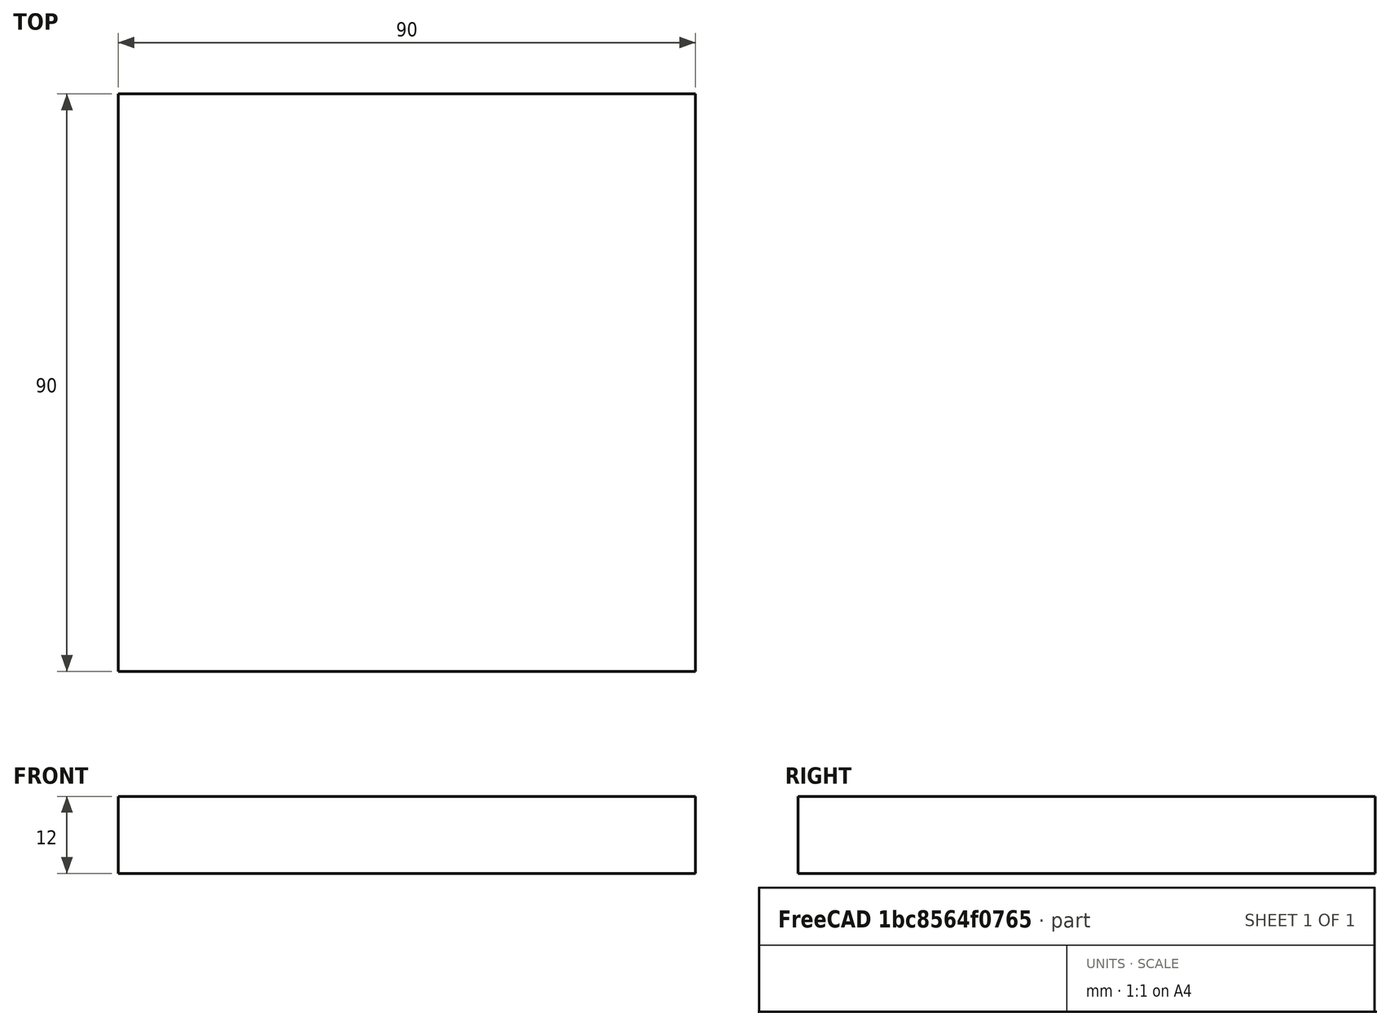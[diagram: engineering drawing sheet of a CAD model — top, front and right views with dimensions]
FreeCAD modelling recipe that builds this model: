
FCSTD DOCUMENT  (FreeCAD 0.18R16146 (Git))
Label: ThreeHoles00
License: All rights reserved
LicenseURL: http://en.wikipedia.org/wiki/All_rights_reserved
objects: Path::FeaturePython×3, Sketcher::SketchObject×2, Part::FeaturePython×2, PartDesign::Pad×1, App::FeaturePython×1, PartDesign::Pocket×1, PartDesign::Body×1, App::DocumentObjectGroup×1, Path::FeatureCompoundPython×1, Mesh::FeaturePython×1
note: 10 computed .brp shape members not serialized (recipe doc carries the construction recipe); baked Part::Feature solids carry a one-line shape summary decoded from their .brp

FEATURE [Sketcher::SketchObject] Sketch
  MapMode = 5
  Support = -> [XY_Plane]
  sketch-geometry (4):
    g0: LineSegment StartX=0 StartY=0 StartZ=0 EndX=70 EndY=0 EndZ=0
    g1: LineSegment StartX=70 StartY=0 StartZ=0 EndX=70 EndY=70 EndZ=0
    g2: LineSegment StartX=70 StartY=70 StartZ=0 EndX=0 EndY=70 EndZ=0
    g3: LineSegment StartX=0 StartY=70 StartZ=0 EndX=0 EndY=0 EndZ=0
  constraints (9):
    c: Coincident(g0,g1)
    c: Coincident(g1,g2)
    c: Coincident(g2,g3)
    c: Coincident(g3,g0)
    c: Horizontal(g0)
    c: Horizontal(g2)
    c: Vertical(g1)
    c: Vertical(g3)
    c: Coincident(g0,g-1)
FEATURE [PartDesign::Pad] Pad
  Length = 10
  Length2 = 100
  Profile = -> Sketch
  Type = 0
FEATURE [App::FeaturePython] SetupSheet  # Path/CAM operation (typed FeaturePython)
  ClearanceHeightExpression = OpStockZMax+SetupSheet.ClearanceHeightOffset
  ClearanceHeightOffset = 5
  FinalDepthExpression = OpFinalDepth
  HorizRapid = 0
  SafeHeightExpression = OpStockZMax+SetupSheet.SafeHeightOffset
  SafeHeightOffset = 3
  StartDepthExpression = OpStartDepth
  StepDownExpression = OpToolDiameter
  VertRapid = 0
FEATURE [Path::FeaturePython] T3__Fraise_6mm  label="T3: Fraise 6mm"  # Path/CAM operation (typed FeaturePython)
  HorizFeed = 5
  HorizRapid = 0
  SpindleDir = 0
  SpindleSpeed = 0
  ToolNumber = 3
  VertFeed = 5
  VertRapid = 0
  expr: HorizRapid = SetupSheet.HorizRapid
  expr: VertRapid = SetupSheet.VertRapid
FEATURE [Sketcher::SketchObject] Sketch001
  MapMode = 5
  Placement = pos=(0,0,10) rot=(0,0,1;0rad)
  Support = -> [Pad]
  sketch-geometry (3):
    g0: Circle CenterX=10 CenterY=20 CenterZ=0 NormalX=0 NormalY=0 NormalZ=1 AngleXU=0 Radius=3.05
    g1: Circle CenterX=10 CenterY=60 CenterZ=0 NormalX=0 NormalY=0 NormalZ=1 AngleXU=0 Radius=3.05
    g2: Circle CenterX=40 CenterY=50 CenterZ=0 NormalX=0 NormalY=0 NormalZ=1 AngleXU=0 Radius=3.05
  constraints (3):
    c: Radius(g0) = 3.05
    c: Equal(g0,g1)
    c: Equal(g0,g2)
FEATURE [PartDesign::Pocket] Pocket
  BaseFeature = -> Pad
  Length = 5
  Length2 = 100
  Profile = -> Sketch001
  Type = 1
FEATURE [PartDesign::Body] Body
  Group = -> [Sketch,Pad,Sketch001,Pocket]
  Origin = -> Origin
  Tip = -> Pocket
FEATURE [Part::FeaturePython] Clone  label="Model-Body"  # Draft clone (typed FeaturePython)
  AttacherType = Attacher::AttachEngine3D
  Fuse = false
  Objects = -> [Body]
  PathResource = Model
  Placement = pos=(10,10,-11) rot=(0,0,1;0rad)
  Scale = (1,1,1)
FEATURE [App::DocumentObjectGroup] Model
  Group = -> [Clone]
FEATURE [Part::FeaturePython] Stock  # WARN: FeaturePython — macro-defined, semantics opaque (R4)
  Base = -> Model
  ExtXneg = 10
  ExtXpos = 10
  ExtYneg = 10
  ExtYpos = 10
  ExtZneg = 1
  ExtZpos = 1
  Placement = pos=(10,10,-11) rot=(0,0,1;0rad)
  StockType = FromBase
FEATURE [Path::FeaturePython] Pocket_Shape  # Path/CAM operation (typed FeaturePython)
  Active = true
  AreaParams:
    Tolerance = 1e-07
    FitArcs = True
    Simplify = False
    CleanDistance = 0.0
    Accuracy = 0.01
    Unit = 1.0
    MinArcPoints = 4
    MaxArcPoints = 100
    ClipperScale = 10000000.0
    Fill = 0
    Coplanar = 0
    Reorient = True
    Outline = False
    Explode = False
    OpenMode = 0
    Deflection = 0.01
    SubjectFill = 0
    ClipFill = 0
    Offset = 0.0
    ExtraPass = 0
    Stepover = 0.0
    LastStepover = 0.0
    JoinType = 0
    EndType = 0
    MiterLimit = 2.0
    RoundPrecision = 0.0
    PocketMode = 1
    ToolRadius = 3.0
    PocketExtraOffset = 0.0
    PocketStepover = 6.0
    PocketLastStepover = 0.0
    FromCenter = True
    Angle = 45.0
    AngleShift = 0.0
    Shift = 0.0
    Thicken = False
    SectionCount = -1
    Stepdown = 1.0
    SectionOffset = 0.0
    SectionTolerance = 1e-06
    SectionMode = 2
    Project = False
  Base = -> [Clone]
  ClearanceHeight = 5
  CutMode = 0
  ExtraOffset = 0
  FinalDepth = -12
  FinishDepth = -12
  KeepToolDown = false
  MinTravel = false
  OffsetPattern = 0
  OpFinalDepth = -11
  OpStartDepth = 0
  OpStockZMax = 0
  OpStockZMin = -12
  OpToolDiameter = 6
  PathParams = {'orientation': 1, 'feedrate': 5.0, 'feedrate_v': 5.0, 'verbose': True, 'resume_height': 3.0, 'retraction': 5.0, 'return_end': True, 'preamble': False}
  SafeHeight = 3
  StartAt = 0
  StartDepth = 1
  StartPoint = (0,0,0)
  StepDown = 4
  StepOver = 100
  ToolController = -> T3__Fraise_6mm
  UseOutline = false
  UseStartPoint = false
  ZigZagAngle = 45
  expr: ClearanceHeight = OpStockZMax + SetupSheet.ClearanceHeightOffset
  expr: SafeHeight = OpStockZMax + SetupSheet.SafeHeightOffset
FEATURE [Path::FeatureCompoundPython] Operations  # Path/CAM operation (typed FeaturePython)
  Group = -> [Pocket_Shape]
  UsePlacements = false
FEATURE [Path::FeaturePython] Job  # Path/CAM operation (typed FeaturePython)
  GeometryTolerance = 0.01
  Model = -> Model
  Operations = -> Operations
  PostProcessor = 10
  PostProcessorOutputFile = /Volumes/SSD/Dev/CNC/MiscCNC/ThreeHoles00.gcode
  SetupSheet = -> SetupSheet
  Stock = -> Stock
  ToolController = -> [T3__Fraise_6mm]
FEATURE [Mesh::FeaturePython] CutMaterial  # WARN: FeaturePython — macro-defined, semantics opaque (R4)
